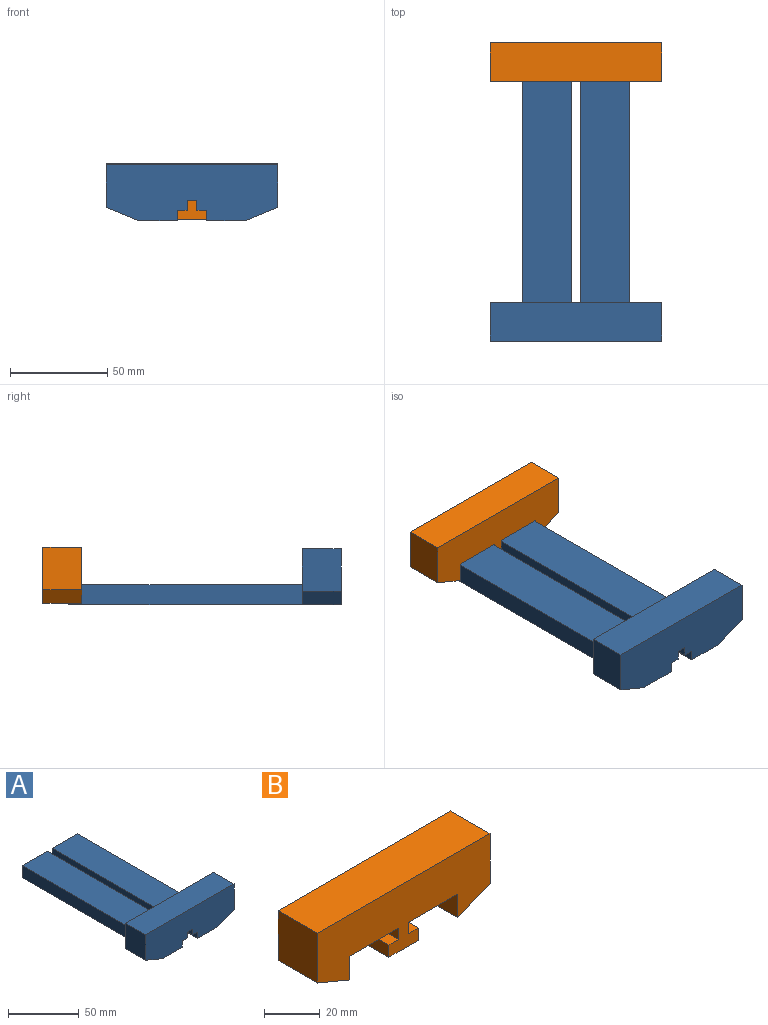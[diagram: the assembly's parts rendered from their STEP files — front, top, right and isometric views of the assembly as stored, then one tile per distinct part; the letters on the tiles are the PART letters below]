
ASSEMBLY  parts=2 mates=1
PART A: 22 faces, bbox 88x140x28.8 mm
  f0: plane 88x28.78mm, normal (0,1,0), area 1848.8mm2, adj f1,f3,f4,f5,f9,f15,f16,f18
  f1: plane 20x5mm, normal (0,0,-1), area 100mm2, adj f0,f10,f12,f13
  f2: plane 140x5.37mm, normal (-1,0,0), area 752.4mm2, adj f8,f10,f11,f20
  f3: plane 21.91x20mm, normal (1,0,0), area 438.1mm2, adj f0,f9,f10,f21
  f4: plane 21.91x20mm, normal (-1,0,0), area 438.1mm2, adj f0,f5,f10,f21
  f5: plane 20x16.5mm, normal (-0.38,0,-0.92), area 357.5mm2, adj f0,f4,f6,f10
  f6: plane 140x20mm, normal (0,0,-1), area 2800mm2, adj f5,f7,f10,f15,f17
  f7: plane 140x5.37mm, normal (1,0,0), area 752.4mm2, adj f6,f10,f14,f17
  f8: plane 140x20mm, normal (0,0,-1), area 2800mm2, adj f2,f9,f10,f18,f20
  f9: plane 20x16.5mm, normal (0.38,0,-0.92), area 357.5mm2, adj f0,f3,f8,f10
  f10: plane 88x28.78mm, normal (0,-1,0), area 2313.7mm2, adj f1,f2,f3,f4,f5,f6,f7,f8
  f11: plane 140x5mm, normal (0,0,-1), area 700mm2, adj f2,f10,f12,f20
  f12: plane 140x5mm, normal (-1,0,0), area 700mm2, adj f1,f10,f11,f19,f20
  f13: plane 140x5mm, normal (1,0,0), area 700mm2, adj f1,f10,f14,f16,f17
  f14: plane 140x5mm, normal (0,0,-1), area 700mm2, adj f7,f10,f13,f17
  f15: plane 120x10.37mm, normal (-1,0,0), area 1244.9mm2, adj f0,f6,f16,f17
  f16: plane 120x25mm, normal (0,0,1), area 3000mm2, adj f0,f13,f15,f17
  f17: plane 25x10.37mm, normal (0,1,0), area 232.5mm2, adj f6,f7,f13,f14,f15,f16
  f18: plane 120x10.37mm, normal (1,0,0), area 1244.9mm2, adj f0,f8,f19,f20
  f19: plane 120x25mm, normal (0,0,1), area 3000mm2, adj f0,f12,f18,f20
  f20: plane 25x10.37mm, normal (0,1,0), area 232.5mm2, adj f2,f8,f11,f12,f18,f19
  f21: plane 88x20mm, normal (0,0,1), area 1760mm2, adj f0,f3,f4,f10
PART B: 20 faces, bbox 88x20x28.8 mm
  f0: plane 25x20mm, normal (0,0,-1), area 500mm2, adj f1,f15,f16,f17
  f1: plane 20x5mm, normal (-1,0,0), area 100mm2, adj f0,f2,f16,f17
  f2: plane 20x5mm, normal (0,0,1), area 100mm2, adj f1,f3,f16,f17
  f3: plane 20x5.37mm, normal (-1,0,0), area 107.5mm2, adj f2,f4,f16,f17
  f4: plane 20x15mm, normal (0,0,-1), area 300mm2, adj f3,f5,f16,f17
  f5: plane 20x5.37mm, normal (1,0,0), area 107.5mm2, adj f4,f6,f16,f17
  f6: plane 20x5mm, normal (0,0,1), area 100mm2, adj f5,f7,f16,f17
  f7: plane 20x5mm, normal (1,0,0), area 100mm2, adj f6,f8,f16,f17
  f8: plane 25x20mm, normal (0,0,-1), area 500mm2, adj f7,f9,f16,f17
  f9: plane 20x10.37mm, normal (-1,0,0), area 207.5mm2, adj f8,f10,f16,f17
  f10: plane 20x16.5mm, normal (0.38,0,-0.92), area 357.5mm2, adj f9,f11,f16,f17
  f11: plane 21.91x20mm, normal (1,0,0), area 438.1mm2, adj f10,f12,f16,f17
  f12: plane 88x20mm, normal (0,0,1), area 1760mm2, adj f11,f13,f16,f17
  f13: plane 21.91x20mm, normal (-1,0,0), area 438.1mm2, adj f12,f14,f16,f17
  f14: plane 20x16.5mm, normal (-0.38,0,-0.92), area 357.5mm2, adj f13,f15,f16,f17
  f15: plane 20x10.37mm, normal (1,0,0), area 207.5mm2, adj f0,f14,f16,f17
  f16: plane 88x28.78mm, normal (0,-1,0), area 1954.4mm2, adj f0,f1,f2,f3,f4,f5,f6,f7
  f17: plane 88x28.78mm, normal (0,1,0), area 1910.2mm2, adj f0,f1,f2,f3,f4,f5,f6,f7
  f18: cylinder r=3.75mm len=7.5mm, axis (0,1,0), area 164.9mm2, adj f17,f19
  f19: plane 7.5x7.5mm, normal (0,1,0), area 44.2mm2, adj f18
PLACE A t=(0,70,0)mm fixed
PLACE B t=(-44,203.38,7.63)mm
MATE slider A.f0 <-> B.f16  axis (0,1,0) through (0,70,17.97)mm
